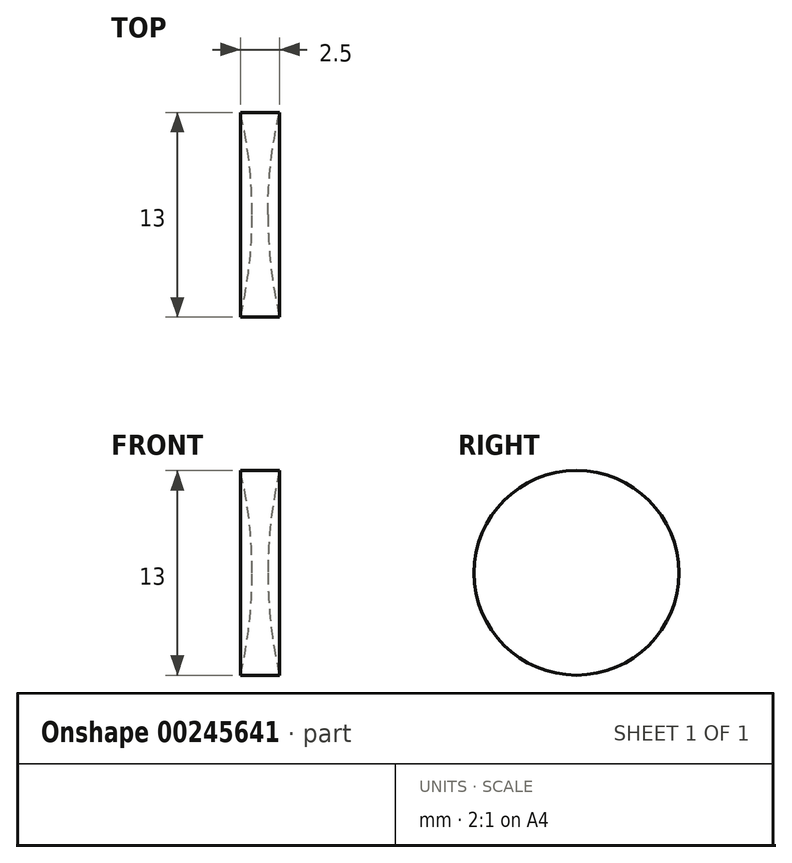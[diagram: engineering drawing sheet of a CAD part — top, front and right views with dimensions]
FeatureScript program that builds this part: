
annotation { "Feature Type Name" : "Feature", "Feature Type Description" : "" }
export const myFeature = defineFeature(function(context is Context, id is Id, definition is map)
    precondition{}
    {
        {
            var Q0;
            Q0=qCreatedBy(makeId("Right.planeOp"),FACE);
            var sketch = newSketch(context, id + "F0", { "sketchPlane" : qUnion([Q0])});
            skCircle(sketch, "E0", {"center": v(0, 0) * mm, "radius": 6.5 * mm});
            skSolve(sketch);
        }
        {
            var Q0;
            Q0 = qSketchRegion(id + "F0", true);
            extrude(context, id + "F1", {"entities" : qUnion([Q0]), "depth" : 2.5 * mm});
        }
        {
            var Q0;
            Q0=qCreatedBy(makeId("Top.planeOp"),FACE);
            var sketch = newSketch(context, id + "F2", { "sketchPlane" : qUnion([Q0])});
            skPoint(sketch, "E1.endSnap0", {"position": v(1.25, 0) * mm});
            skLineSegment(sketch, "E2", {"start": v(0, 0) * mm, "end": v(0, -6.5) * mm});
            skArc(sketch, "E3", {"start": v(0, -6.5) * mm, "mid": v(0.56, -3.27) * mm, "end": v(0.75, 0) * mm});
            skLineSegment(sketch, "E4", {"start": v(2.5, 0) * mm, "end": v(2.5, -6.5) * mm});
            skLineSegment(sketch, "E5", {"start": v(2.5, -6.5) * mm, "end": v(2.5, 0) * mm});
            skArc(sketch, "E6", {"start": v(1.75, 0) * mm, "mid": v(1.94, -3.27) * mm, "end": v(2.5, -6.5) * mm});
            skPoint(sketch, "E7.orphan", {"position": v(2.5, 6.5) * mm});
            skPoint(sketch, "E8.end.orphan", {"position": v(0, 6.5) * mm});
            skLineSegment(sketch, "E9", {"start": v(1.75, 0) * mm, "end": v(2.5, 0) * mm});
            skLineSegment(sketch, "E10", {"start": v(0.75, 0) * mm, "end": v(0, 0) * mm});
            skLineSegment(sketch, "E11", {"start": v(0, 0) * mm, "end": v(2.5, 0) * mm, "construction": true});
            skSolve(sketch);
        }
        {
            var Q0;
            Q0 = qSketchRegion(id + "F2", true);
            var Q1;
            Q1=sQuery(id+"F2.wireOp",EDGE,"E11");
            revolve(context, id + "F3", {"operationType" : NewBodyOperationType.REMOVE, "entities" : qUnion([Q0]), "axis" : qUnion([Q1]), "revolveType" : RevolveType.FULL, "oppositeDirection" : true});
        }
    });
